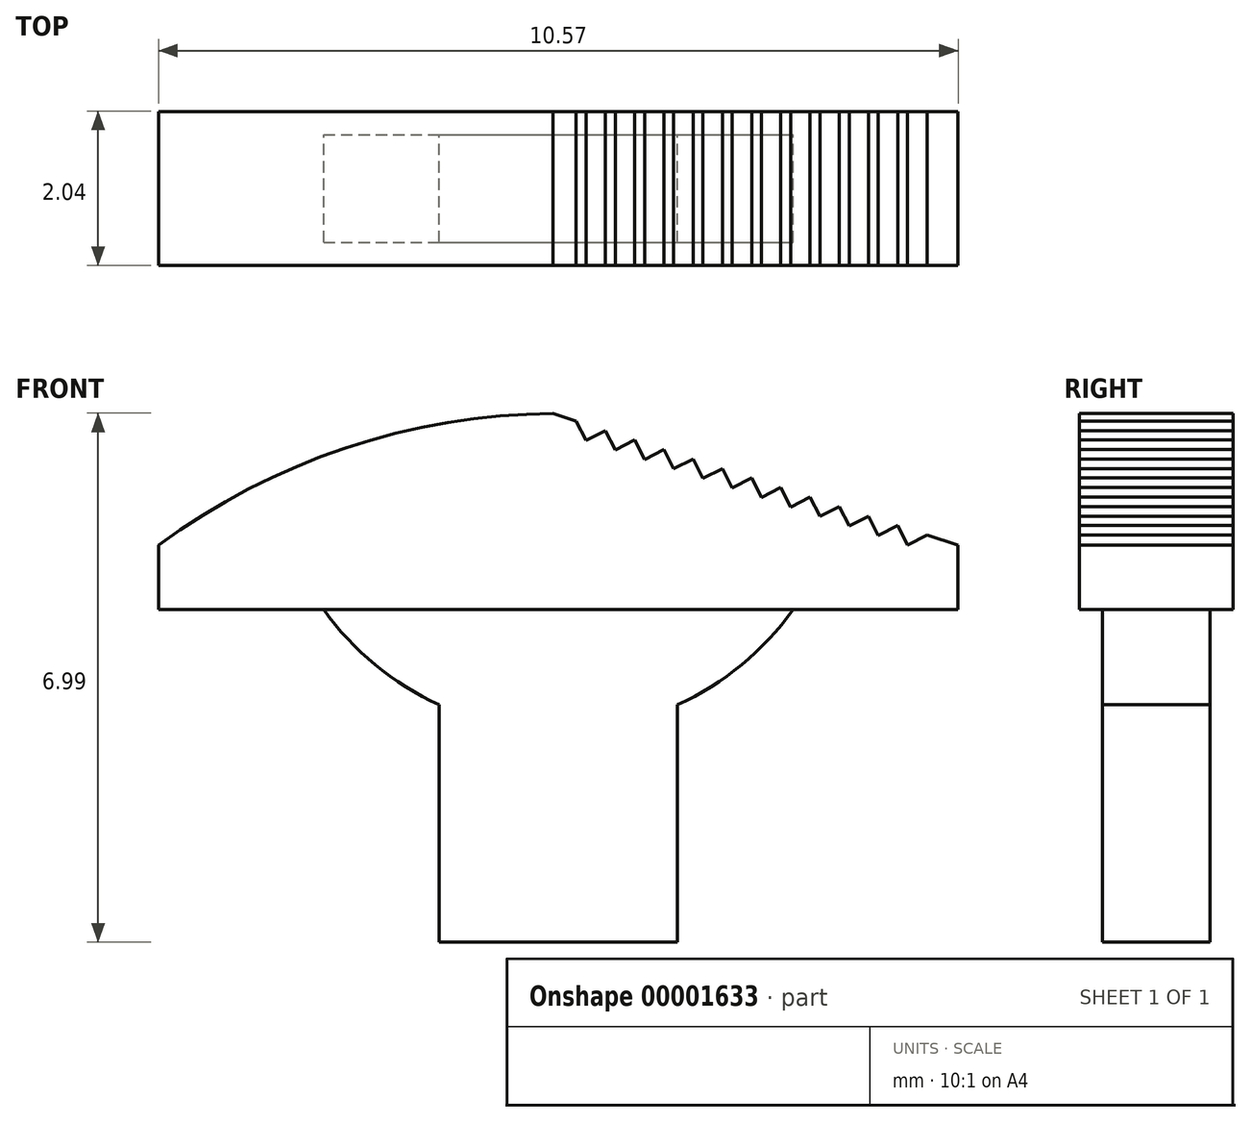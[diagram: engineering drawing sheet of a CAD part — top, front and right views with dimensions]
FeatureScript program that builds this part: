
annotation { "Feature Type Name" : "Feature", "Feature Type Description" : "" }
export const myFeature = defineFeature(function(context is Context, id is Id, definition is map)
    precondition{}
    {
        {
            var Q0;
            Q0=qCreatedBy(makeId("Front.planeOp"),FACE);
            var sketch = newSketch(context, id + "F0", { "sketchPlane" : qUnion([Q0])});
            skLineSegment(sketch, "E0", {"start": v(0, 0) * mm, "end": v(3.15, 0) * mm});
            skLineSegment(sketch, "E1", {"start": v(3.15, 0) * mm, "end": v(3.15, 3.13) * mm});
            skLineSegment(sketch, "E2", {"start": v(0, 0) * mm, "end": v(0, 3.13) * mm});
            skArc(sketch, "E3", {"start": v(-1.53, 4.4) * mm, "mid": v(-0.85, 3.66) * mm, "end": v(0, 3.13) * mm});
            skPoint(sketch, "E4", {"position": v(1.57, 0) * mm});
            skLineSegment(sketch, "E5", {"start": v(-3.7, 4.4) * mm, "end": v(-1.53, 4.4) * mm});
            skPoint(sketch, "E6", {"position": v(1.57, 4.4) * mm});
            skLineSegment(sketch, "E7", {"start": v(-3.7, 4.4) * mm, "end": v(-3.7, 5.25) * mm});
            skLineSegment(sketch, "E8", {"start": v(6.86, 4.4) * mm, "end": v(6.86, 5.25) * mm});
            skArc(sketch, "E9", {"start": v(1.5, 6.99) * mm, "mid": v(-1.24, 6.53) * mm, "end": v(-3.7, 5.25) * mm});
            skPoint(sketch, "E10", {"position": v(1.5, 6.99) * mm});
            skArc(sketch, "E11.trimOffspring", {"start": v(3.15, 3.13) * mm, "mid": v(4, 3.66) * mm, "end": v(4.68, 4.4) * mm});
            skLineSegment(sketch, "E12.trimOffspring", {"start": v(4.68, 4.4) * mm, "end": v(6.86, 4.4) * mm});
            skLineSegment(sketch, "E13", {"start": v(6.86, 5.25) * mm, "end": v(1.5, 6.99) * mm});
            skLineSegment(sketch, "E14", {"start": v(-1.53, 4.4) * mm, "end": v(4.68, 4.4) * mm});
            skSolve(sketch);
        }
        {
            var Q0;
            Q0=makeQuery(id+"F0.imprint","IMPRINT",FACE,{"disambiguationData":[TD([[makeQuery(id+"F0.imprint","IMPRINT",EDGE,{"derivedFrom":sQuery(id+"F0.wireOp",EDGE,"E5")}),1.0]])]});
            extrude(context, id + "F1", {"entities" : qUnion([Q0]), "endBound" : BoundingType.SYMMETRIC, "depth" : 2.03 * mm});
        }
        {
            var Q0;
            Q0=makeQuery(id+"F0.imprint","IMPRINT",FACE,{"disambiguationData":[TD([[makeQuery(id+"F0.imprint","IMPRINT",EDGE,{"derivedFrom":sQuery(id+"F0.wireOp",EDGE,"E0")}),1.0]])]});
            extrude(context, id + "F2", {"entities" : qUnion([Q0]), "operationType" : NewBodyOperationType.ADD, "endBound" : BoundingType.SYMMETRIC, "depth" : 1.42 * mm});
        }
        {
            var Q0;
            Q0=makeQuery(id+"F1.opExtrude","CAP_FACE",FACE,{"disambiguationData":[OSD([sQuery(id+"F0.wireOp",EDGE,"E5"),sQuery(id+"F0.wireOp",EDGE,"E7"),sQuery(id+"F0.wireOp",EDGE,"E8"),sQuery(id+"F0.wireOp",EDGE,"E9"),sQuery(id+"F0.wireOp",EDGE,"E12.trimOffspring"),sQuery(id+"F0.wireOp",EDGE,"E13"),sQuery(id+"F0.wireOp",EDGE,"E14")])],"isStart":false});
            var sketch = newSketch(context, id + "F3", { "sketchPlane" : qUnion([Q0])});
            skLineSegment(sketch, "E15", {"start": v(6.86, 5.25) * mm, "end": v(6.45, 5.38) * mm, "construction": true});
            skLineSegment(sketch, "E16", {"start": v(6.45, 5.38) * mm, "end": v(6.06, 5.5) * mm});
            skLineSegment(sketch, "E17", {"start": v(6.06, 5.5) * mm, "end": v(6.2, 5.25) * mm});
            skLineSegment(sketch, "E18", {"start": v(6.2, 5.25) * mm, "end": v(6.45, 5.38) * mm});
            skLineSegment(sketch, "E19", {"start": v(6.06, 5.5) * mm, "end": v(5.67, 5.63) * mm});
            skLineSegment(sketch, "E20", {"start": v(5.67, 5.63) * mm, "end": v(5.29, 5.76) * mm});
            skLineSegment(sketch, "E21", {"start": v(5.29, 5.76) * mm, "end": v(4.9, 5.88) * mm});
            skLineSegment(sketch, "E22", {"start": v(4.9, 5.88) * mm, "end": v(4.51, 6) * mm});
            skLineSegment(sketch, "E23", {"start": v(4.51, 6) * mm, "end": v(4.13, 6.13) * mm});
            skLineSegment(sketch, "E24", {"start": v(4.13, 6.13) * mm, "end": v(3.74, 6.26) * mm});
            skLineSegment(sketch, "E25", {"start": v(3.74, 6.26) * mm, "end": v(3.36, 6.38) * mm});
            skLineSegment(sketch, "E26", {"start": v(3.36, 6.38) * mm, "end": v(2.97, 6.5) * mm});
            skLineSegment(sketch, "E27", {"start": v(2.97, 6.5) * mm, "end": v(2.58, 6.63) * mm});
            skLineSegment(sketch, "E28", {"start": v(2.58, 6.63) * mm, "end": v(2.2, 6.76) * mm});
            skLineSegment(sketch, "E29", {"start": v(2.2, 6.76) * mm, "end": v(1.8, 6.89) * mm});
            skLineSegment(sketch, "E30", {"start": v(6.06, 5.5) * mm, "end": v(5.8, 5.37) * mm});
            skLineSegment(sketch, "E31", {"start": v(5.8, 5.37) * mm, "end": v(5.67, 5.63) * mm});
            skLineSegment(sketch, "E32", {"start": v(5.67, 5.63) * mm, "end": v(5.42, 5.5) * mm});
            skLineSegment(sketch, "E33", {"start": v(5.42, 5.5) * mm, "end": v(5.29, 5.76) * mm});
            skLineSegment(sketch, "E34", {"start": v(5.29, 5.76) * mm, "end": v(5.03, 5.62) * mm});
            skLineSegment(sketch, "E35", {"start": v(5.03, 5.62) * mm, "end": v(4.9, 5.88) * mm});
            skLineSegment(sketch, "E36", {"start": v(4.9, 5.88) * mm, "end": v(4.65, 5.75) * mm});
            skLineSegment(sketch, "E37", {"start": v(4.65, 5.75) * mm, "end": v(4.51, 6) * mm});
            skLineSegment(sketch, "E38", {"start": v(4.51, 6) * mm, "end": v(4.26, 5.88) * mm});
            skLineSegment(sketch, "E39", {"start": v(4.26, 5.88) * mm, "end": v(4.13, 6.13) * mm});
            skLineSegment(sketch, "E40", {"start": v(4.13, 6.13) * mm, "end": v(3.87, 6) * mm});
            skLineSegment(sketch, "E41", {"start": v(3.87, 6) * mm, "end": v(3.74, 6.26) * mm});
            skLineSegment(sketch, "E42", {"start": v(3.74, 6.26) * mm, "end": v(3.49, 6.13) * mm});
            skLineSegment(sketch, "E43", {"start": v(3.49, 6.13) * mm, "end": v(3.36, 6.38) * mm});
            skLineSegment(sketch, "E44", {"start": v(3.36, 6.38) * mm, "end": v(3.1, 6.25) * mm});
            skLineSegment(sketch, "E45", {"start": v(3.1, 6.25) * mm, "end": v(2.97, 6.5) * mm});
            skLineSegment(sketch, "E46", {"start": v(2.97, 6.5) * mm, "end": v(2.71, 6.38) * mm});
            skLineSegment(sketch, "E47", {"start": v(2.71, 6.38) * mm, "end": v(2.58, 6.63) * mm});
            skLineSegment(sketch, "E48", {"start": v(2.58, 6.63) * mm, "end": v(2.33, 6.5) * mm});
            skLineSegment(sketch, "E49", {"start": v(2.33, 6.5) * mm, "end": v(2.2, 6.76) * mm});
            skLineSegment(sketch, "E50", {"start": v(2.2, 6.76) * mm, "end": v(1.94, 6.63) * mm});
            skLineSegment(sketch, "E51", {"start": v(1.94, 6.63) * mm, "end": v(1.8, 6.89) * mm});
            skSolve(sketch);
        }
        {
            var Q0;
            Q0=makeQuery(id+"F3.imprint","IMPRINT",FACE,{"disambiguationData":[TD([[makeQuery(id+"F3.imprint","IMPRINT",EDGE,{"derivedFrom":sQuery(id+"F3.wireOp",EDGE,"E16")}),1.0]])]});
            var Q1;
            Q1=makeQuery(id+"F3.imprint","IMPRINT",FACE,{"disambiguationData":[TD([[makeQuery(id+"F3.imprint","IMPRINT",EDGE,{"derivedFrom":sQuery(id+"F3.wireOp",EDGE,"E19")}),1.0]])]});
            var Q2;
            Q2=makeQuery(id+"F3.imprint","IMPRINT",FACE,{"disambiguationData":[TD([[makeQuery(id+"F3.imprint","IMPRINT",EDGE,{"derivedFrom":sQuery(id+"F3.wireOp",EDGE,"E20")}),1.0]])]});
            var Q3;
            Q3=makeQuery(id+"F3.imprint","IMPRINT",FACE,{"disambiguationData":[TD([[makeQuery(id+"F3.imprint","IMPRINT",EDGE,{"derivedFrom":sQuery(id+"F3.wireOp",EDGE,"E21")}),1.0]])]});
            var Q4;
            Q4=makeQuery(id+"F3.imprint","IMPRINT",FACE,{"disambiguationData":[TD([[makeQuery(id+"F3.imprint","IMPRINT",EDGE,{"derivedFrom":sQuery(id+"F3.wireOp",EDGE,"E22")}),1.0]])]});
            var Q5;
            Q5=makeQuery(id+"F3.imprint","IMPRINT",FACE,{"disambiguationData":[TD([[makeQuery(id+"F3.imprint","IMPRINT",EDGE,{"derivedFrom":sQuery(id+"F3.wireOp",EDGE,"E23")}),1.0]])]});
            var Q6;
            Q6=makeQuery(id+"F3.imprint","IMPRINT",FACE,{"disambiguationData":[TD([[makeQuery(id+"F3.imprint","IMPRINT",EDGE,{"derivedFrom":sQuery(id+"F3.wireOp",EDGE,"E24")}),1.0]])]});
            var Q7;
            Q7=makeQuery(id+"F3.imprint","IMPRINT",FACE,{"disambiguationData":[TD([[makeQuery(id+"F3.imprint","IMPRINT",EDGE,{"derivedFrom":sQuery(id+"F3.wireOp",EDGE,"E25")}),1.0]])]});
            var Q8;
            Q8=makeQuery(id+"F3.imprint","IMPRINT",FACE,{"disambiguationData":[TD([[makeQuery(id+"F3.imprint","IMPRINT",EDGE,{"derivedFrom":sQuery(id+"F3.wireOp",EDGE,"E26")}),1.0]])]});
            var Q9;
            Q9=makeQuery(id+"F3.imprint","IMPRINT",FACE,{"disambiguationData":[TD([[makeQuery(id+"F3.imprint","IMPRINT",EDGE,{"derivedFrom":sQuery(id+"F3.wireOp",EDGE,"E28")}),1.0]])]});
            var Q10;
            Q10=makeQuery(id+"F3.imprint","IMPRINT",FACE,{"disambiguationData":[TD([[makeQuery(id+"F3.imprint","IMPRINT",EDGE,{"derivedFrom":sQuery(id+"F3.wireOp",EDGE,"E29")}),1.0]])]});
            var Q11;
            Q11=makeQuery(id+"F3.imprint","IMPRINT",FACE,{"disambiguationData":[TD([[makeQuery(id+"F3.imprint","IMPRINT",EDGE,{"derivedFrom":sQuery(id+"F3.wireOp",EDGE,"E27")}),1.0]])]});
            extrude(context, id + "F4", {"entities" : qUnion([Q0, Q1, Q2, Q3, Q4, Q5, Q6, Q7, Q8, Q9, Q10, Q11]), "operationType" : NewBodyOperationType.REMOVE, "endBound" : BoundingType.THROUGH_ALL, "oppositeDirection" : true, "depth" : 25.4 * mm});
        }
    });
